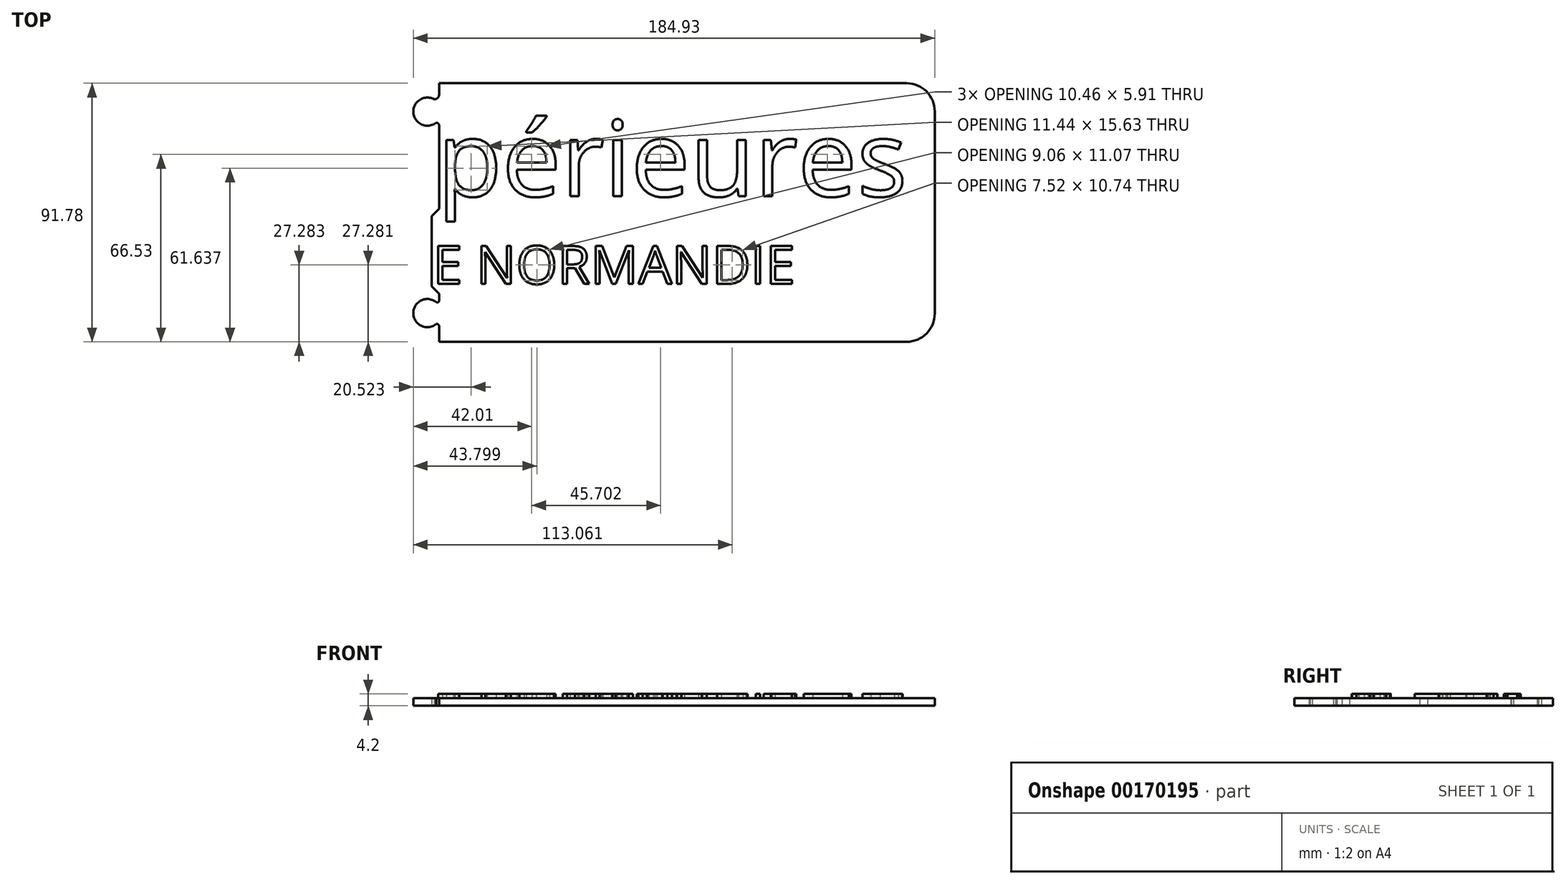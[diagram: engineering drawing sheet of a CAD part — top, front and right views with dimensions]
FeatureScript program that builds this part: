
annotation { "Feature Type Name" : "Feature", "Feature Type Description" : "" }
export const myFeature = defineFeature(function(context is Context, id is Id, definition is map)
    precondition{}
    {
        {
            var Q0;
            Q0=qCreatedBy(makeId("Top.planeOp"),FACE);
            var sketch = newSketch(context, id + "F0", { "sketchPlane" : qUnion([Q0])});
            skLineSegment(sketch, "E0.bottom", {"start": v(-153.76, 79.26) * mm, "end": v(196.24, 79.26) * mm});
            skLineSegment(sketch, "E0.top", {"start": v(-153.76, -13.12) * mm, "end": v(196.24, -13.12) * mm});
            skLineSegment(sketch, "E0.left", {"start": v(-153.76, 79.26) * mm, "end": v(-153.76, -13.12) * mm});
            skLineSegment(sketch, "E0.right", {"start": v(196.24, 79.26) * mm, "end": v(196.24, -13.12) * mm});
            skCircle(sketch, "E1", {"center": v(-123.39, 12.33) * mm, "radius": 17.49 * mm});
            skCircle(sketch, "E2", {"center": v(-123.39, 12.33) * mm, "radius": 11.88 * mm});
            skCircle(sketch, "E3", {"center": v(-123.39, 12.33) * mm, "radius": 9.49 * mm});
            skCircle(sketch, "E4", {"center": v(-123.39, 12.33) * mm, "radius": 3.6 * mm});
            skCircle(sketch, "E5", {"center": v(-123.39, 12.33) * mm, "radius": 7.83 * mm});
            skCircle(sketch, "E6", {"center": v(-123.39, 12.33) * mm, "radius": 13.72 * mm});
            skLineSegment(sketch, "E7", {"start": v(-123.39, 12.33) * mm, "end": v(-116.12, 28.24) * mm});
            skLineSegment(sketch, "E8", {"start": v(-112.54, -1.39) * mm, "end": v(-121.72, 9.15) * mm});
            skCircle(sketch, "E9", {"center": v(-123.39, 12.33) * mm, "radius": 18.48 * mm});
            skLineSegment(sketch, "E10", {"start": v(-118.04, 18.06) * mm, "end": v(-113.59, 28) * mm});
            skLineSegment(sketch, "E11", {"start": v(-118.04, 18.06) * mm, "end": v(-107.93, 22.47) * mm});
            skLineSegment(sketch, "E12", {"start": v(-116.5, 16.06) * mm, "end": v(-111.14, 18.51) * mm});
            skLineSegment(sketch, "E13", {"start": v(-117.25, 7.47) * mm, "end": v(-113.21, 3.13) * mm});
            skText(sketch, "E14", { "text": "Ecoles Supérieures", "fontName": "OpenSans-Regular.ttf"});
            skText(sketch, "E15", { "text": "CCI PORTES DE NORMANDIE", "fontName": "OpenSans-Regular.ttf"});
            const initialGuessF0  = {"E14": [-0.14265, 0.03824, 1, 0, 0.02692], "E15": [-0.10308, 0.00715, 1, 0, 0.01356]};
            skSetInitialGuess(sketch, initialGuessF0);
            skSolve(sketch);
        }
        {
            var Q0;
            Q0=makeQuery(id+"F0.imprint","IMPRINT",FACE,{"disambiguationData":[TD([[makeQuery(id+"F0.imprint","IMPRINT",EDGE,{"derivedFrom":sQuery(id+"F0.wireOp",EDGE,"E14.sketch_text.stroke-0")}),-1.0]])]});
            var Q1;
            Q1=makeQuery(id+"F0.imprint","IMPRINT",FACE,{"disambiguationData":[TD([[makeQuery(id+"F0.imprint","IMPRINT",EDGE,{"derivedFrom":sQuery(id+"F0.wireOp",EDGE,"E14.sketch_text.stroke-12")}),-1.0]])]});
            var Q2;
            Q2=makeQuery(id+"F0.imprint","IMPRINT",FACE,{"disambiguationData":[TD([[makeQuery(id+"F0.imprint","IMPRINT",EDGE,{"derivedFrom":sQuery(id+"F0.wireOp",EDGE,"E14.sketch_text.stroke-27")}),-1.0]])]});
            var Q3;
            Q3=makeQuery(id+"F0.imprint","IMPRINT",FACE,{"disambiguationData":[TD([[makeQuery(id+"F0.imprint","IMPRINT",EDGE,{"derivedFrom":sQuery(id+"F0.wireOp",EDGE,"E14.sketch_text.stroke-44")}),-1.0]])]});
            var Q4;
            Q4=makeQuery(id+"F0.imprint","IMPRINT",FACE,{"disambiguationData":[TD([[makeQuery(id+"F0.imprint","IMPRINT",EDGE,{"derivedFrom":sQuery(id+"F0.wireOp",EDGE,"E14.sketch_text.stroke-48")}),-1.0]])]});
            var Q5;
            Q5=makeQuery(id+"F0.imprint","IMPRINT",FACE,{"disambiguationData":[TD([[makeQuery(id+"F0.imprint","IMPRINT",EDGE,{"derivedFrom":sQuery(id+"F0.wireOp",EDGE,"E14.sketch_text.stroke-67")}),-1.0]])]});
            var Q6;
            Q6=makeQuery(id+"F0.imprint","IMPRINT",FACE,{"disambiguationData":[TD([[makeQuery(id+"F0.imprint","IMPRINT",EDGE,{"derivedFrom":sQuery(id+"F0.wireOp",EDGE,"E14.sketch_text.stroke-92")}),-1.0]])]});
            var Q7;
            Q7=makeQuery(id+"F0.imprint","IMPRINT",FACE,{"disambiguationData":[TD([[makeQuery(id+"F0.imprint","IMPRINT",EDGE,{"derivedFrom":sQuery(id+"F0.wireOp",EDGE,"E14.sketch_text.stroke-117")}),-1.0]])]});
            var Q8;
            Q8=makeQuery(id+"F0.imprint","IMPRINT",FACE,{"disambiguationData":[TD([[makeQuery(id+"F0.imprint","IMPRINT",EDGE,{"derivedFrom":sQuery(id+"F0.wireOp",EDGE,"E14.sketch_text.stroke-134")}),-1.0]])]});
            var Q9;
            Q9=makeQuery(id+"F0.imprint","IMPRINT",FACE,{"disambiguationData":[TD([[makeQuery(id+"F0.imprint","IMPRINT",EDGE,{"derivedFrom":sQuery(id+"F0.wireOp",EDGE,"E15.sketch_text.stroke-34")}),-1.0]])]});
            var Q10;
            Q10=makeQuery(id+"F0.imprint","IMPRINT",FACE,{"disambiguationData":[TD([[makeQuery(id+"F0.imprint","IMPRINT",EDGE,{"derivedFrom":sQuery(id+"F0.wireOp",EDGE,"E15.sketch_text.stroke-49")}),-1.0]])]});
            var Q11;
            Q11=makeQuery(id+"F0.imprint","IMPRINT",FACE,{"disambiguationData":[TD([[makeQuery(id+"F0.imprint","IMPRINT",EDGE,{"derivedFrom":sQuery(id+"F0.wireOp",EDGE,"E15.sketch_text.stroke-65")}),-1.0]])]});
            var Q12;
            Q12=makeQuery(id+"F0.imprint","IMPRINT",FACE,{"disambiguationData":[TD([[makeQuery(id+"F0.imprint","IMPRINT",EDGE,{"derivedFrom":sQuery(id+"F0.wireOp",EDGE,"E15.sketch_text.stroke-83")}),-1.0]])]});
            var Q13;
            Q13=makeQuery(id+"F0.imprint","IMPRINT",FACE,{"disambiguationData":[TD([[makeQuery(id+"F0.imprint","IMPRINT",EDGE,{"derivedFrom":sQuery(id+"F0.wireOp",EDGE,"E15.sketch_text.stroke-91")}),-1.0]])]});
            var Q14;
            Q14=makeQuery(id+"F0.imprint","IMPRINT",FACE,{"disambiguationData":[TD([[makeQuery(id+"F0.imprint","IMPRINT",EDGE,{"derivedFrom":sQuery(id+"F0.wireOp",EDGE,"E15.sketch_text.stroke-0")}),-1.0]])]});
            var Q15;
            Q15=makeQuery(id+"F0.imprint","IMPRINT",FACE,{"disambiguationData":[TD([[makeQuery(id+"F0.imprint","IMPRINT",EDGE,{"derivedFrom":sQuery(id+"F0.wireOp",EDGE,"E15.sketch_text.stroke-15")}),-1.0]])]});
            var Q16;
            Q16=makeQuery(id+"F0.imprint","IMPRINT",FACE,{"disambiguationData":[TD([[makeQuery(id+"F0.imprint","IMPRINT",EDGE,{"derivedFrom":sQuery(id+"F0.wireOp",EDGE,"E15.sketch_text.stroke-30")}),-1.0]])]});
            var Q17;
            Q17=makeQuery(id+"F0.imprint","IMPRINT",FACE,{"disambiguationData":[TD([[makeQuery(id+"F0.imprint","IMPRINT",EDGE,{"derivedFrom":sQuery(id+"F0.wireOp",EDGE,"E14.sketch_text.stroke-159")}),-1.0]])]});
            var Q18;
            Q18=makeQuery(id+"F0.imprint","IMPRINT",FACE,{"disambiguationData":[TD([[makeQuery(id+"F0.imprint","IMPRINT",EDGE,{"derivedFrom":sQuery(id+"F0.wireOp",EDGE,"E14.sketch_text.stroke-178")}),-1.0]])]});
            var Q19;
            Q19=makeQuery(id+"F0.imprint","IMPRINT",FACE,{"disambiguationData":[TD([[makeQuery(id+"F0.imprint","IMPRINT",EDGE,{"derivedFrom":sQuery(id+"F0.wireOp",EDGE,"E14.sketch_text.stroke-186")}),-1.0]])]});
            var Q20;
            Q20=makeQuery(id+"F0.imprint","IMPRINT",FACE,{"disambiguationData":[TD([[makeQuery(id+"F0.imprint","IMPRINT",EDGE,{"derivedFrom":sQuery(id+"F0.wireOp",EDGE,"E14.sketch_text.stroke-230")}),-1.0]])]});
            var Q21;
            Q21=makeQuery(id+"F0.imprint","IMPRINT",FACE,{"disambiguationData":[TD([[makeQuery(id+"F0.imprint","IMPRINT",EDGE,{"derivedFrom":sQuery(id+"F0.wireOp",EDGE,"E14.sketch_text.stroke-247")}),-1.0]])]});
            var Q22;
            Q22=makeQuery(id+"F0.imprint","IMPRINT",FACE,{"disambiguationData":[TD([[makeQuery(id+"F0.imprint","IMPRINT",EDGE,{"derivedFrom":sQuery(id+"F0.wireOp",EDGE,"E14.sketch_text.stroke-279")}),-1.0]])]});
            var Q23;
            Q23=makeQuery(id+"F0.imprint","IMPRINT",FACE,{"disambiguationData":[TD([[makeQuery(id+"F0.imprint","IMPRINT",EDGE,{"derivedFrom":sQuery(id+"F0.wireOp",EDGE,"E14.sketch_text.stroke-260")}),-1.0]])]});
            var Q24;
            Q24=makeQuery(id+"F0.imprint","IMPRINT",FACE,{"disambiguationData":[TD([[makeQuery(id+"F0.imprint","IMPRINT",EDGE,{"derivedFrom":sQuery(id+"F0.wireOp",EDGE,"E14.sketch_text.stroke-211")}),-1.0]])]});
            var Q25;
            Q25=makeQuery(id+"F0.imprint","IMPRINT",FACE,{"disambiguationData":[TD([[makeQuery(id+"F0.imprint","IMPRINT",EDGE,{"derivedFrom":sQuery(id+"F0.wireOp",EDGE,"E14.sketch_text.stroke-199")}),-1.0]])]});
            var Q26;
            Q26=makeQuery(id+"F0.imprint","IMPRINT",FACE,{"disambiguationData":[TD([[makeQuery(id+"F0.imprint","IMPRINT",EDGE,{"derivedFrom":sQuery(id+"F0.wireOp",EDGE,"E14.sketch_text.stroke-203")}),-1.0]])]});
            var Q27;
            Q27=makeQuery(id+"F0.imprint","IMPRINT",FACE,{"disambiguationData":[TD([[makeQuery(id+"F0.imprint","IMPRINT",EDGE,{"derivedFrom":sQuery(id+"F0.wireOp",EDGE,"E15.sketch_text.stroke-263")}),-1.0]])]});
            var Q28;
            Q28=makeQuery(id+"F0.imprint","IMPRINT",FACE,{"disambiguationData":[TD([[makeQuery(id+"F0.imprint","IMPRINT",EDGE,{"derivedFrom":sQuery(id+"F0.wireOp",EDGE,"E15.sketch_text.stroke-267")}),-1.0]])]});
            var Q29;
            Q29=makeQuery(id+"F0.imprint","IMPRINT",FACE,{"disambiguationData":[TD([[makeQuery(id+"F0.imprint","IMPRINT",EDGE,{"derivedFrom":sQuery(id+"F0.wireOp",EDGE,"E15.sketch_text.stroke-249")}),-1.0]])]});
            var Q30;
            Q30=makeQuery(id+"F0.imprint","IMPRINT",FACE,{"disambiguationData":[TD([[makeQuery(id+"F0.imprint","IMPRINT",EDGE,{"derivedFrom":sQuery(id+"F0.wireOp",EDGE,"E15.sketch_text.stroke-103")}),-1.0]])]});
            var Q31;
            Q31=makeQuery(id+"F0.imprint","IMPRINT",FACE,{"disambiguationData":[TD([[makeQuery(id+"F0.imprint","IMPRINT",EDGE,{"derivedFrom":sQuery(id+"F0.wireOp",EDGE,"E15.sketch_text.stroke-128")}),-1.0]])]});
            var Q32;
            Q32=makeQuery(id+"F0.imprint","IMPRINT",FACE,{"disambiguationData":[TD([[makeQuery(id+"F0.imprint","IMPRINT",EDGE,{"derivedFrom":sQuery(id+"F0.wireOp",EDGE,"E15.sketch_text.stroke-154")}),-1.0]])]});
            var Q33;
            Q33=makeQuery(id+"F0.imprint","IMPRINT",FACE,{"disambiguationData":[TD([[makeQuery(id+"F0.imprint","IMPRINT",EDGE,{"derivedFrom":sQuery(id+"F0.wireOp",EDGE,"E15.sketch_text.stroke-142")}),-1.0]])]});
            var Q34;
            Q34=makeQuery(id+"F0.imprint","IMPRINT",FACE,{"disambiguationData":[TD([[makeQuery(id+"F0.imprint","IMPRINT",EDGE,{"derivedFrom":sQuery(id+"F0.wireOp",EDGE,"E15.sketch_text.stroke-169")}),-1.0]])]});
            var Q35;
            Q35=makeQuery(id+"F0.imprint","IMPRINT",FACE,{"disambiguationData":[TD([[makeQuery(id+"F0.imprint","IMPRINT",EDGE,{"derivedFrom":sQuery(id+"F0.wireOp",EDGE,"E15.sketch_text.stroke-185")}),-1.0]])]});
            var Q36;
            Q36=makeQuery(id+"F0.imprint","IMPRINT",FACE,{"disambiguationData":[TD([[makeQuery(id+"F0.imprint","IMPRINT",EDGE,{"derivedFrom":sQuery(id+"F0.wireOp",EDGE,"E15.sketch_text.stroke-203")}),-1.0]])]});
            var Q37;
            Q37=makeQuery(id+"F0.imprint","IMPRINT",FACE,{"disambiguationData":[TD([[makeQuery(id+"F0.imprint","IMPRINT",EDGE,{"derivedFrom":sQuery(id+"F0.wireOp",EDGE,"E15.sketch_text.stroke-234")}),-1.0]])]});
            var Q38;
            Q38=makeQuery(id+"F0.imprint","IMPRINT",FACE,{"disambiguationData":[TD([[makeQuery(id+"F0.imprint","IMPRINT",EDGE,{"derivedFrom":sQuery(id+"F0.wireOp",EDGE,"E15.sketch_text.stroke-221")}),-1.0]])]});
            var Q39;
            {var subQ0=sQuery(id+"F0.wireOp",EDGE,"E8");var subQ1=sQuery(id+"F0.wireOp",EDGE,"E4");var subQ2=makeQuery(id+"F0.imprint","INTERSECT",VERTEX,{"derivedFrom":[subQ1,subQ0]});Q39=makeQuery(id+"F0.imprint","IMPRINT",FACE,{"disambiguationData":[TD([[makeQuery(id+"F0.imprint","IMPRINT",EDGE,{"disambiguationData":[TD([[subQ2,1.0]])],"derivedFrom":subQ1}),-1.0]])]});}
            var Q40;
            {var subQ0=sQuery(id+"F0.wireOp",EDGE,"E7");var subQ1=sQuery(id+"F0.wireOp",EDGE,"E3");var subQ2=makeQuery(id+"F0.imprint","INTERSECT",VERTEX,{"derivedFrom":[subQ1,subQ0]});Q40=makeQuery(id+"F0.imprint","IMPRINT",FACE,{"disambiguationData":[TD([[makeQuery(id+"F0.imprint","IMPRINT",EDGE,{"disambiguationData":[TD([[subQ2,-1.0]])],"derivedFrom":subQ1}),1.0]])]});}
            var Q41;
            {var subQ0=sQuery(id+"F0.wireOp",EDGE,"E7");var subQ1=sQuery(id+"F0.wireOp",EDGE,"E2");var subQ2=makeQuery(id+"F0.imprint","INTERSECT",VERTEX,{"derivedFrom":[subQ1,subQ0]});Q41=makeQuery(id+"F0.imprint","IMPRINT",FACE,{"disambiguationData":[TD([[makeQuery(id+"F0.imprint","IMPRINT",EDGE,{"disambiguationData":[TD([[subQ2,-1.0]])],"derivedFrom":subQ1}),-1.0]])]});}
            var Q42;
            {var subQ0=sQuery(id+"F0.wireOp",EDGE,"E7");var subQ1=sQuery(id+"F0.wireOp",EDGE,"E1");var subQ2=makeQuery(id+"F0.imprint","INTERSECT",VERTEX,{"derivedFrom":[subQ1,subQ0]});Q42=makeQuery(id+"F0.imprint","IMPRINT",FACE,{"disambiguationData":[TD([[makeQuery(id+"F0.imprint","IMPRINT",EDGE,{"disambiguationData":[TD([[subQ2,-1.0]])],"derivedFrom":subQ1}),1.0]])]});}
            extrude(context, id + "F1", {"entities" : qUnion([Q0, Q1, Q2, Q3, Q4, Q5, Q6, Q7, Q8, Q9, Q10, Q11, Q12, Q13, Q14, Q15, Q16, Q17, Q18, Q19, Q20, Q21, Q22, Q23, Q24, Q25, Q26, Q27, Q28, Q29, Q30, Q31, Q32, Q33, Q34, Q35, Q36, Q37, Q38, Q39, Q40, Q41, Q42]), "depth" : 1.5 * mm});
        }
        {
            var Q0;
            Q0=makeQuery(id+"F0.imprint","IMPRINT",FACE,{"disambiguationData":[TD([[makeQuery(id+"F0.imprint","IMPRINT",EDGE,{"derivedFrom":sQuery(id+"F0.wireOp",EDGE,"E0.bottom")}),-1.0]])]});
            var sketch = newSketch(context, id + "F2", { "sketchPlane" : qUnion([Q0])});
            skLineSegment(sketch, "E16.bottom", {"start": v(-154.27, -13.4) * mm, "end": v(196.36, -13.4) * mm});
            skLineSegment(sketch, "E16.top", {"start": v(-154.27, 78.37) * mm, "end": v(196.36, 78.37) * mm});
            skLineSegment(sketch, "E16.left", {"start": v(-154.27, -13.4) * mm, "end": v(-154.27, 78.37) * mm});
            skLineSegment(sketch, "E16.right", {"start": v(196.36, -13.4) * mm, "end": v(196.36, 78.37) * mm});
            skSolve(sketch);
        }
        {
            var Q0;
            Q0=qSketchRegion(id+"F2",true);
            var Q1;
            {var subQ5=makeQuery(id+"F0.imprint","IMPRINT",EDGE,{"derivedFrom":sQuery(id+"F0.wireOp",EDGE,"E0.top")});Q1=makeQuery(id+"F2.imprint","IMPRINT",FACE,{"disambiguationData":[TD([[makeQuery(id+"F2.imprint","IMPRINT",EDGE,{"derivedFrom":subQ5}),1.0]])]});}
            extrude(context, id + "F3", {"entities" : qUnion([Q0, Q1]), "oppositeDirection" : true, "depth" : 2.7 * mm});
        }
        {
            var Q0;
            Q0=makeQuery(id+"F3.opExtrude","SWEPT_EDGE",EDGE,{"disambiguationData":[OSD([sQuery(id+"F2.wireOp",EDGE,"E16.bottom"),sQuery(id+"F2.wireOp",EDGE,"E16.right")])]});
            var Q1;
            Q1=makeQuery(id+"F3.opExtrude","SWEPT_EDGE",EDGE,{"disambiguationData":[OSD([sQuery(id+"F2.wireOp",EDGE,"E16.top"),sQuery(id+"F2.wireOp",EDGE,"E16.right")])]});
            var Q2;
            Q2=makeQuery(id+"F3.opExtrude","SWEPT_EDGE",EDGE,{"disambiguationData":[OSD([sQuery(id+"F2.wireOp",EDGE,"E16.bottom"),sQuery(id+"F2.wireOp",EDGE,"E16.left")])]});
            var Q3;
            Q3=makeQuery(id+"F3.opExtrude","SWEPT_EDGE",EDGE,{"disambiguationData":[OSD([sQuery(id+"F2.wireOp",EDGE,"E16.top"),sQuery(id+"F2.wireOp",EDGE,"E16.left")])]});
            fillet(context, id + "F4", {"entities" : qUnion([Q0, Q1, Q2, Q3]), "radius" : 10 * mm, "tangentPropagation" : true, "allowEdgeOverflow" : false});
        }
        {
            var Q0;
            {var subQ0=sQuery(id+"F0.wireOp",EDGE,"E12");var subQ1=sQuery(id+"F0.wireOp",EDGE,"E3");var subQ2=makeQuery(id+"F0.imprint","INTERSECT",VERTEX,{"derivedFrom":[subQ1,subQ0]});Q0=makeQuery(id+"F0.imprint","IMPRINT",FACE,{"disambiguationData":[TD([[makeQuery(id+"F0.imprint","IMPRINT",EDGE,{"disambiguationData":[TD([[subQ2,1.0]])],"derivedFrom":subQ1}),1.0]])]});}
            var Q1;
            {var subQ0=sQuery(id+"F0.wireOp",EDGE,"E12");var subQ1=sQuery(id+"F0.wireOp",EDGE,"E2");var subQ2=makeQuery(id+"F0.imprint","INTERSECT",VERTEX,{"derivedFrom":[subQ1,subQ0]});Q1=makeQuery(id+"F0.imprint","IMPRINT",FACE,{"disambiguationData":[TD([[makeQuery(id+"F0.imprint","IMPRINT",EDGE,{"disambiguationData":[TD([[subQ2,1.0]])],"derivedFrom":subQ1}),1.0]])]});}
            var Q2;
            {var subQ0=sQuery(id+"F0.wireOp",EDGE,"E12");var subQ1=sQuery(id+"F0.wireOp",EDGE,"E2");var subQ2=makeQuery(id+"F0.imprint","INTERSECT",VERTEX,{"derivedFrom":[subQ1,subQ0]});Q2=makeQuery(id+"F0.imprint","IMPRINT",FACE,{"disambiguationData":[TD([[makeQuery(id+"F0.imprint","IMPRINT",EDGE,{"disambiguationData":[TD([[subQ2,1.0]])],"derivedFrom":subQ1}),-1.0]])]});}
            var Q3;
            {var subQ0=sQuery(id+"F0.wireOp",EDGE,"E11");var subQ1=sQuery(id+"F0.wireOp",EDGE,"E3");var subQ2=makeQuery(id+"F0.imprint","INTERSECT",VERTEX,{"derivedFrom":[subQ1,subQ0]});Q3=makeQuery(id+"F0.imprint","IMPRINT",FACE,{"disambiguationData":[TD([[makeQuery(id+"F0.imprint","IMPRINT",EDGE,{"disambiguationData":[TD([[subQ2,-1.0]])],"derivedFrom":subQ1}),1.0]])]});}
            var Q4;
            {var subQ0=sQuery(id+"F0.wireOp",EDGE,"E11");var subQ1=sQuery(id+"F0.wireOp",EDGE,"E2");var subQ2=makeQuery(id+"F0.imprint","INTERSECT",VERTEX,{"derivedFrom":[subQ1,subQ0]});Q4=makeQuery(id+"F0.imprint","IMPRINT",FACE,{"disambiguationData":[TD([[makeQuery(id+"F0.imprint","IMPRINT",EDGE,{"disambiguationData":[TD([[subQ2,-1.0]])],"derivedFrom":subQ1}),1.0]])]});}
            var Q5;
            {var subQ0=sQuery(id+"F0.wireOp",EDGE,"E10");var subQ1=sQuery(id+"F0.wireOp",EDGE,"E1");var subQ2=makeQuery(id+"F0.imprint","INTERSECT",VERTEX,{"derivedFrom":[subQ1,subQ0]});Q5=makeQuery(id+"F0.imprint","IMPRINT",FACE,{"disambiguationData":[TD([[makeQuery(id+"F0.imprint","IMPRINT",EDGE,{"disambiguationData":[TD([[subQ2,1.0]])],"derivedFrom":subQ1}),1.0]])]});}
            var Q6;
            {var subQ0=sQuery(id+"F0.wireOp",EDGE,"E10");var subQ1=sQuery(id+"F0.wireOp",EDGE,"E1");var subQ2=makeQuery(id+"F0.imprint","INTERSECT",VERTEX,{"derivedFrom":[subQ1,subQ0]});Q6=makeQuery(id+"F0.imprint","IMPRINT",FACE,{"disambiguationData":[TD([[makeQuery(id+"F0.imprint","IMPRINT",EDGE,{"disambiguationData":[TD([[subQ2,1.0]])],"derivedFrom":subQ1}),-1.0]])]});}
            var Q7;
            {var subQ0=sQuery(id+"F0.wireOp",EDGE,"E11");var subQ1=sQuery(id+"F0.wireOp",EDGE,"E2");var subQ2=makeQuery(id+"F0.imprint","INTERSECT",VERTEX,{"derivedFrom":[subQ1,subQ0]});Q7=makeQuery(id+"F0.imprint","IMPRINT",FACE,{"disambiguationData":[TD([[makeQuery(id+"F0.imprint","IMPRINT",EDGE,{"disambiguationData":[TD([[subQ2,-1.0]])],"derivedFrom":subQ1}),-1.0]])]});}
            extrude(context, id + "F5", {"entities" : qUnion([Q0, Q1, Q2, Q3, Q4, Q5, Q6, Q7]), "oppositeDirection" : true, "depth" : 2 * mm, "hasSecondDirection" : true, "secondDirectionOppositeDirection" : false, "secondDirectionDepth" : 1.5 * mm});
        }
        {
            var Q0;
            Q0=makeQuery(id+"F3.opExtrude","CAP_FACE",FACE,{"disambiguationData":[OSD([sQuery(id+"F2.wireOp",EDGE,"E16.bottom"),sQuery(id+"F2.wireOp",EDGE,"E16.top"),sQuery(id+"F2.wireOp",EDGE,"E16.left"),sQuery(id+"F2.wireOp",EDGE,"E16.right")])],"isStart":false});
            var sketch = newSketch(context, id + "F6", { "sketchPlane" : qUnion([Q0])});
            skLineSegment(sketch, "E17.bottom", {"start": v(-160.63, 19.31) * mm, "end": v(201.75, 19.31) * mm});
            skLineSegment(sketch, "E17.top", {"start": v(-160.63, -87.06) * mm, "end": v(201.75, -87.06) * mm});
            skLineSegment(sketch, "E17.left", {"start": v(-160.63, 19.31) * mm, "end": v(-160.63, -87.06) * mm});
            skLineSegment(sketch, "E17.right", {"start": v(201.75, 19.31) * mm, "end": v(201.75, -87.06) * mm});
            skLineSegment(sketch, "E18", {"start": v(20.56, 19.31) * mm, "end": v(20.56, -87.06) * mm});
            skCircle(sketch, "E19", {"center": v(16.43, -68.3) * mm, "radius": 5 * mm});
            skCircle(sketch, "E20", {"center": v(16.43, -68.3) * mm, "radius": 4.9 * mm});
            skCircle(sketch, "E21", {"center": v(16.43, 3.22) * mm, "radius": 5 * mm});
            skCircle(sketch, "E22", {"center": v(16.43, 3.22) * mm, "radius": 4.9 * mm});
            skLineSegment(sketch, "E23", {"start": v(17.94, -6.24) * mm, "end": v(17.94, -31.13) * mm});
            skLineSegment(sketch, "E24", {"start": v(17.94, -31.13) * mm, "end": v(20.56, -33.87) * mm});
            skLineSegment(sketch, "E25", {"start": v(17.94, -6.24) * mm, "end": v(20.56, -3.58) * mm});
            skArc(sketch, "E26", {"start": v(20.56, -74.23) * mm, "mid": v(19.84, -72.96) * mm, "end": v(18.4, -72.79) * mm});
            skArc(sketch, "E27", {"start": v(19.05, -64.16) * mm, "mid": v(19.97, -64.29) * mm, "end": v(20.56, -63.57) * mm});
            skArc(sketch, "E28", {"start": v(20.56, -1.3) * mm, "mid": v(20.19, -0.63) * mm, "end": v(19.42, -0.66) * mm});
            skArc(sketch, "E29", {"start": v(19.26, 7.21) * mm, "mid": v(20.1, 7.1) * mm, "end": v(20.56, 7.81) * mm});
            skSolve(sketch);
        }
        {
            var Q0;
            {var subQ10=sQuery(id+"F6.wireOp",EDGE,"E17.left");Q0=makeQuery(id+"F6.imprint","IMPRINT",FACE,{"disambiguationData":[TD([[makeQuery(id+"F6.imprint","IMPRINT",EDGE,{"derivedFrom":subQ10}),1.0]])]});}
            var Q1;
            Q1=makeQuery(id+"F6.imprint","IMPRINT",FACE,{"disambiguationData":[TD([[makeQuery(id+"F6.imprint","IMPRINT",EDGE,{"derivedFrom":sQuery(id+"F6.wireOp",EDGE,"E23")}),-1.0]])]});
            extrude(context, id + "F7", {"entities" : qUnion([Q0, Q1]), "operationType" : NewBodyOperationType.REMOVE, "oppositeDirection" : true, "depth" : 25 * mm});
        }
    });
